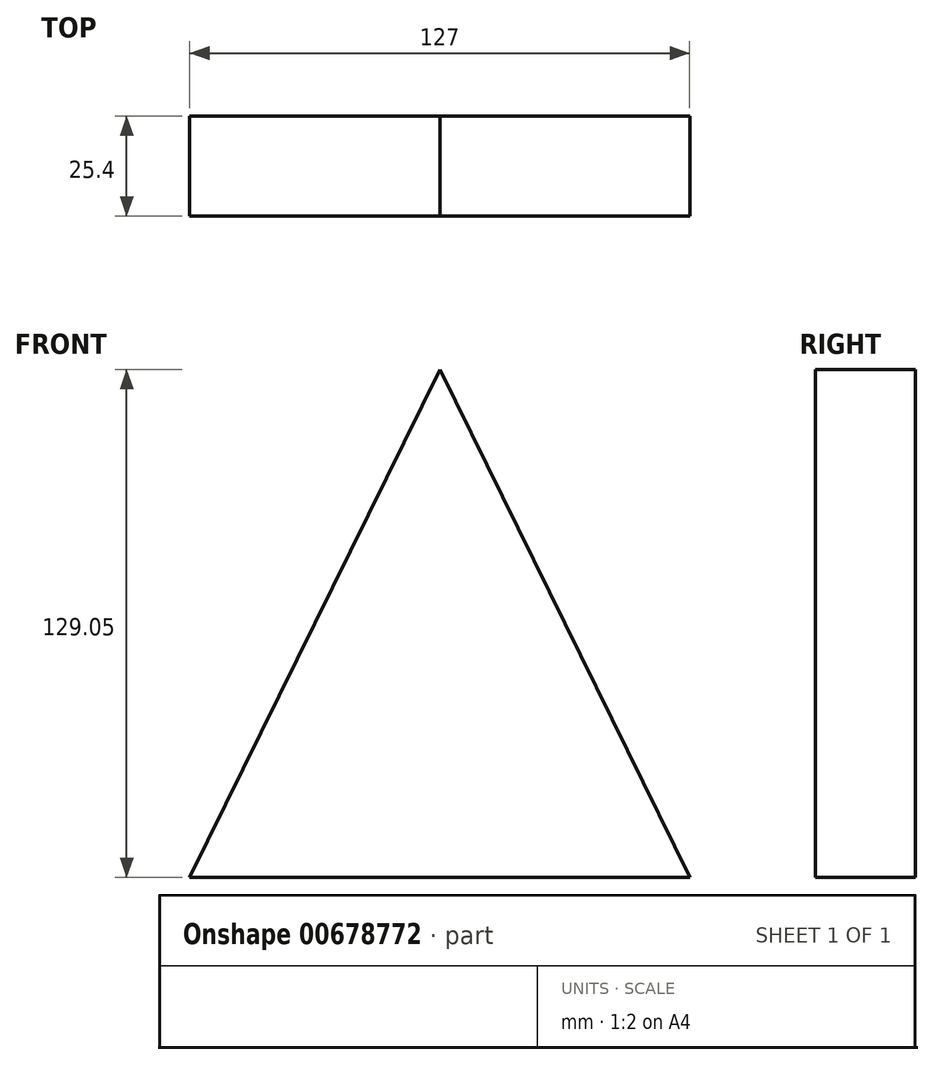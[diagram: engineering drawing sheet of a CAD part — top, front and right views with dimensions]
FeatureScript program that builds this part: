
annotation { "Feature Type Name" : "Feature", "Feature Type Description" : "" }
export const myFeature = defineFeature(function(context is Context, id is Id, definition is map)
    precondition{}
    {
        {
            var Q0;
            Q0=qCreatedBy(makeId("Front.planeOp"),FACE);
            var sketch = newSketch(context, id + "F0", { "sketchPlane" : qUnion([Q0])});
            skLineSegment(sketch, "E0.top", {"start": v(-72.14, -61) * mm, "end": v(54.86, -61) * mm});
            skLineSegment(sketch, "E1", {"start": v(-8.64, 68.06) * mm, "end": v(54.86, -61) * mm});
            skLineSegment(sketch, "E2", {"start": v(-8.64, 68.06) * mm, "end": v(-72.14, -61) * mm});
            skPoint(sketch, "E0.left.start.orphan", {"position": v(-72.14, 68.06) * mm});
            skPoint(sketch, "E0.right.start.orphan", {"position": v(54.86, 68.06) * mm});
            skSolve(sketch);
        }
        {
            var Q0;
            Q0 = qSketchRegion(id + "F0", true);
            extrude(context, id + "F1", {"entities" : qUnion([Q0]), "depth" : 25.4 * mm, "offsetDistance" : 25.4 * mm});
        }
    });
